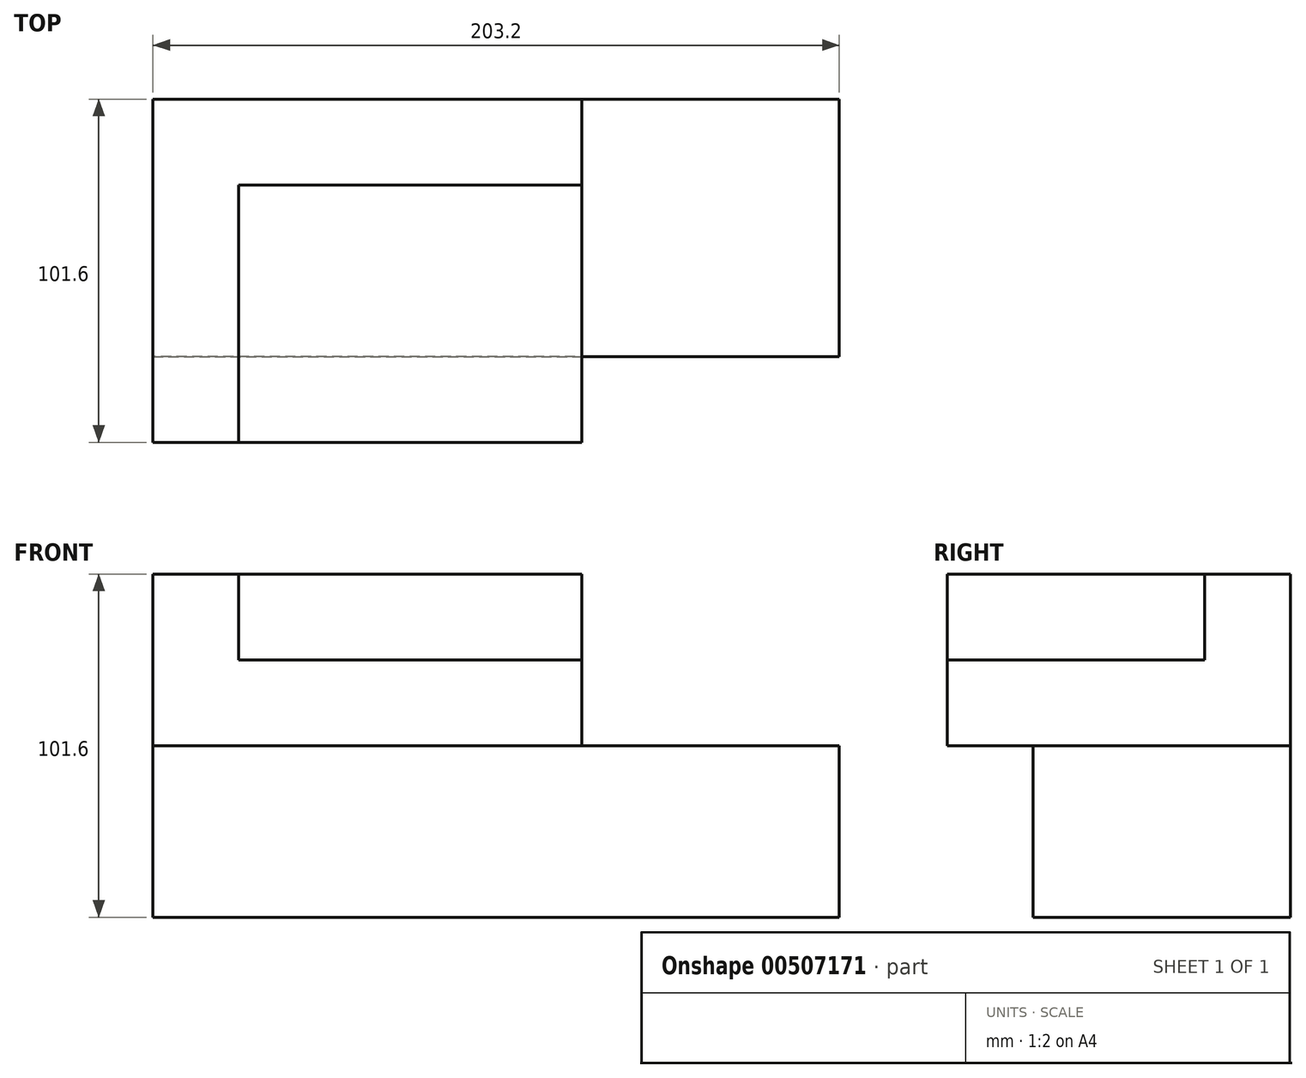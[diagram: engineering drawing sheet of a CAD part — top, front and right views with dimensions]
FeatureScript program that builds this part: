
annotation { "Feature Type Name" : "Feature", "Feature Type Description" : "" }
export const myFeature = defineFeature(function(context is Context, id is Id, definition is map)
    precondition{}
    {
        {
            var Q0;
            Q0=qCreatedBy(makeId("Front.planeOp"),FACE);
            var sketch = newSketch(context, id + "F0", { "sketchPlane" : qUnion([Q0])});
            skLineSegment(sketch, "E0", {"start": v(-127, 37.75) * mm, "end": v(0, 37.75) * mm});
            skLineSegment(sketch, "E1", {"start": v(0, 37.75) * mm, "end": v(0, -13.05) * mm});
            skLineSegment(sketch, "E2", {"start": v(0, -13.05) * mm, "end": v(76.2, -13.05) * mm});
            skLineSegment(sketch, "E3", {"start": v(76.2, -13.05) * mm, "end": v(76.2, -63.85) * mm});
            skLineSegment(sketch, "E4", {"start": v(76.2, -63.85) * mm, "end": v(-127, -63.85) * mm});
            skLineSegment(sketch, "E5", {"start": v(-127, -63.85) * mm, "end": v(-127, 37.75) * mm});
            skSolve(sketch);
        }
        {
            var Q0;
            Q0 = qSketchRegion(id + "F0", true);
            extrude(context, id + "F1", {"entities" : qUnion([Q0]), "depth" : 101.6 * mm});
        }
        {
            var Q0;
            Q0=makeQuery(id+"F1.opExtrude","SWEPT_FACE",FACE,{"disambiguationData":[OSD([sQuery(id+"F0.wireOp",EDGE,"E0")])]});
            var sketch = newSketch(context, id + "F2", { "sketchPlane" : qUnion([Q0])});
            skLineSegment(sketch, "E6.bottom", {"start": v(-101.6, -25.4) * mm, "end": v(0, -25.4) * mm});
            skLineSegment(sketch, "E6.top", {"start": v(-101.6, -101.6) * mm, "end": v(0, -101.6) * mm});
            skLineSegment(sketch, "E6.left", {"start": v(-101.6, -25.4) * mm, "end": v(-101.6, -101.6) * mm});
            skLineSegment(sketch, "E6.right", {"start": v(0, -25.4) * mm, "end": v(0, -101.6) * mm});
            skSolve(sketch);
        }
        {
            var Q0;
            Q0 = qSketchRegion(id + "F2", true);
            extrude(context, id + "F3", {"entities" : qUnion([Q0]), "operationType" : NewBodyOperationType.REMOVE, "oppositeDirection" : true, "depth" : 25.4 * mm});
        }
        {
            var Q0;
            Q0=makeQuery(id+"F1.opExtrude","CAP_FACE",FACE,{"disambiguationData":[OSD([sQuery(id+"F0.wireOp",EDGE,"E0"),sQuery(id+"F0.wireOp",EDGE,"E1"),sQuery(id+"F0.wireOp",EDGE,"E2"),sQuery(id+"F0.wireOp",EDGE,"E3"),sQuery(id+"F0.wireOp",EDGE,"E4"),sQuery(id+"F0.wireOp",EDGE,"E5")])],"isStart":false});
            var sketch = newSketch(context, id + "F4", { "sketchPlane" : qUnion([Q0])});
            skLineSegment(sketch, "E7.bottom", {"start": v(76.2, -13.05) * mm, "end": v(-127, -13.05) * mm});
            skLineSegment(sketch, "E7.top", {"start": v(76.2, -63.85) * mm, "end": v(-127, -63.85) * mm});
            skLineSegment(sketch, "E7.left", {"start": v(76.2, -13.05) * mm, "end": v(76.2, -63.85) * mm});
            skLineSegment(sketch, "E7.right", {"start": v(-127, -13.05) * mm, "end": v(-127, -63.85) * mm});
            skSolve(sketch);
        }
        {
            var Q0;
            Q0 = qSketchRegion(id + "F4", true);
            extrude(context, id + "F5", {"entities" : qUnion([Q0]), "operationType" : NewBodyOperationType.REMOVE, "oppositeDirection" : true, "depth" : 25.4 * mm});
        }
    });
